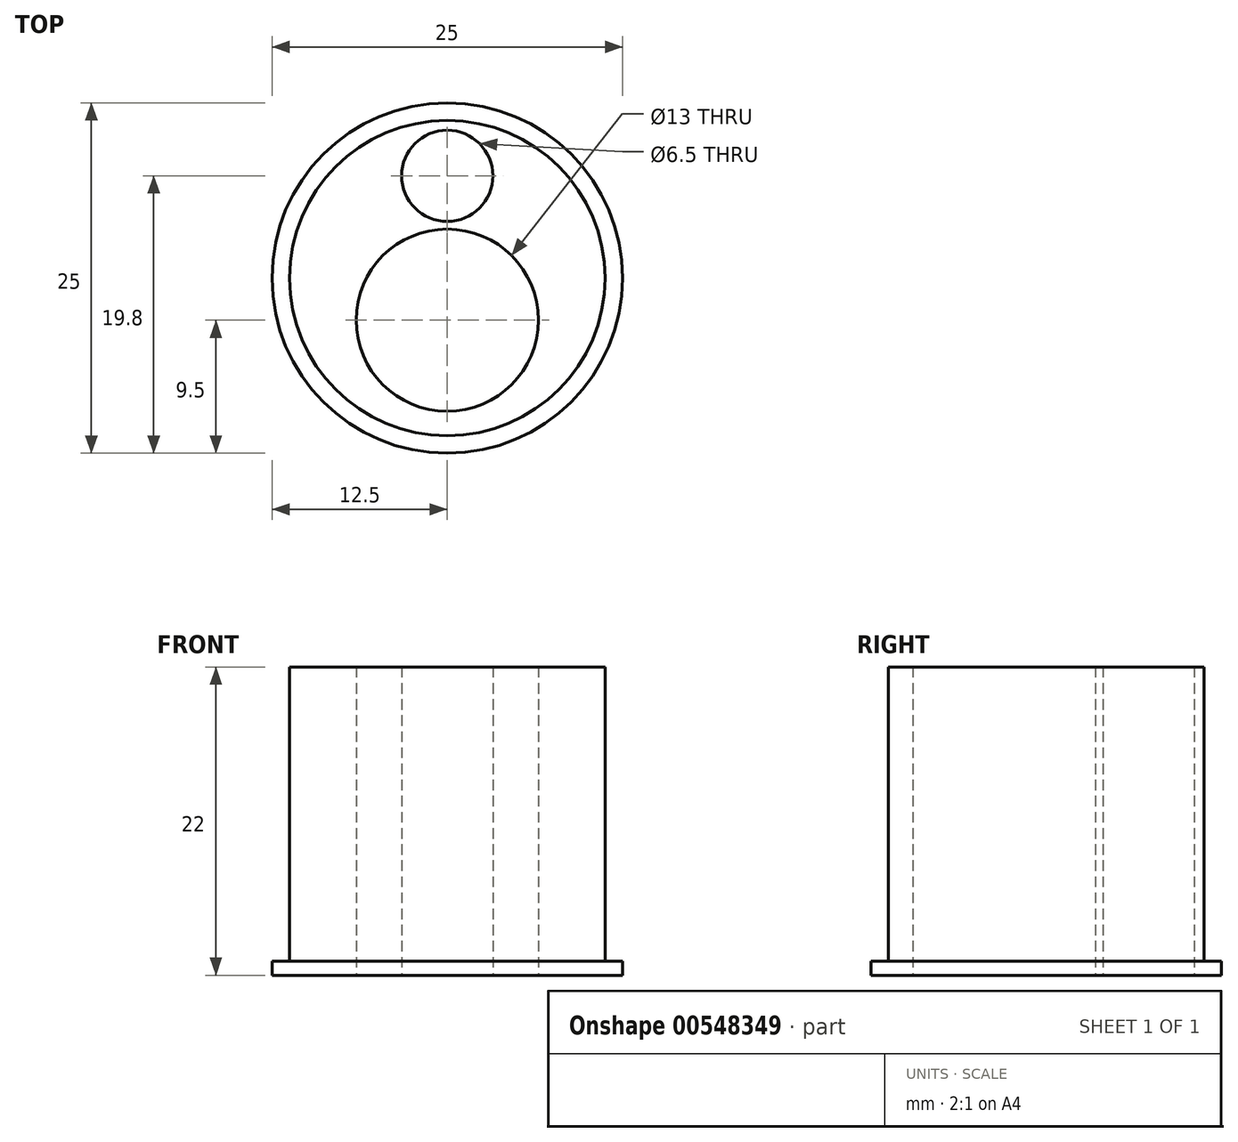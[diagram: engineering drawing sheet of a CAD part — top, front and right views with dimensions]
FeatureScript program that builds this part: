
annotation { "Feature Type Name" : "Feature", "Feature Type Description" : "" }
export const myFeature = defineFeature(function(context is Context, id is Id, definition is map)
    precondition{}
    {
        {
            var Q0;
            Q0=qCreatedBy(makeId("Top.planeOp"),FACE);
            var sketch = newSketch(context, id + "F0", { "sketchPlane" : qUnion([Q0])});
            skCircle(sketch, "E0", {"center": v(0, 0) * mm, "radius": 11.25 * mm});
            skCircle(sketch, "E1", {"center": v(0, -3) * mm, "radius": 6.5 * mm});
            skCircle(sketch, "E2", {"center": v(0, 0) * mm, "radius": 12.5 * mm});
            skCircle(sketch, "E3", {"center": v(0, 7.3) * mm, "radius": 3.25 * mm});
            skSolve(sketch);
        }
        {
            var Q0;
            Q0=makeQuery(id+"F0.imprint","IMPRINT",FACE,{"disambiguationData":[TD([[makeQuery(id+"F0.imprint","IMPRINT",EDGE,{"derivedFrom":sQuery(id+"F0.wireOp",EDGE,"E0")}),1.0]])]});
            extrude(context, id + "F1", {"entities" : qUnion([Q0]), "depth" : 22 * mm, "offsetDistance" : 25 * mm});
        }
        {
            var Q0;
            Q0 = qSketchRegion(id + "F0", true);
            extrude(context, id + "F2", {"entities" : qUnion([Q0]), "operationType" : NewBodyOperationType.ADD, "depth" : 1 * mm, "offsetDistance" : 25 * mm});
        }
    });
